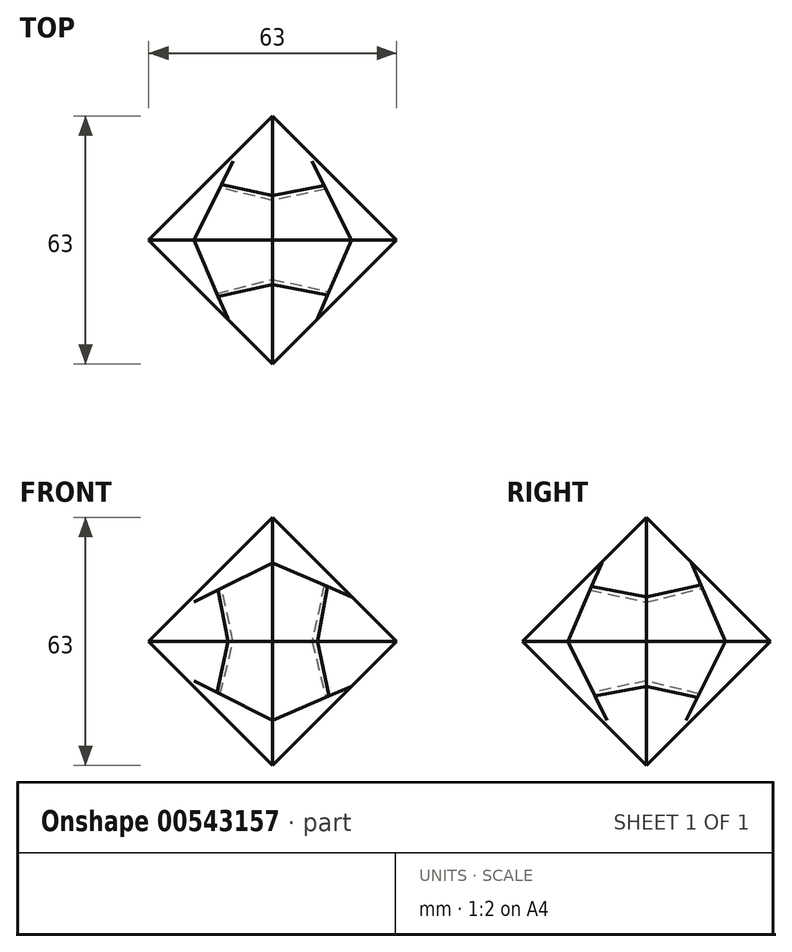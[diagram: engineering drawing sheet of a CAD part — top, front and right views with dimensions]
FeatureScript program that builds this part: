
annotation { "Feature Type Name" : "Feature", "Feature Type Description" : "" }
export const myFeature = defineFeature(function(context is Context, id is Id, definition is map)
    precondition{}
    {
        {
            var Q0;
            Q0=qCreatedBy(makeId("Front.planeOp"),FACE);
            var sketch = newSketch(context, id + "F0", { "sketchPlane" : qUnion([Q0])});
            skLineSegment(sketch, "E0", {"start": v(46.28, 0) * mm, "end": v(0, 20) * mm});
            skLineSegment(sketch, "E1", {"start": v(0, 20) * mm, "end": v(-40, 0) * mm});
            skLineSegment(sketch, "E2", {"start": v(-40, 0) * mm, "end": v(0, -20) * mm});
            skLineSegment(sketch, "E3", {"start": v(0, -20) * mm, "end": v(46.28, 0) * mm});
            skSolve(sketch);
        }
        {
            var Q0;
            Q0=makeQuery(id+"F0.imprint","IMPRINT",FACE,{"disambiguationData":[TD([[makeQuery(id+"F0.imprint","IMPRINT",EDGE,{"derivedFrom":sQuery(id+"F0.wireOp",EDGE,"E0")}),1.0]])]});
            extrude(context, id + "F1", {"entities" : qUnion([Q0]), "depth" : 25 * mm, "offsetDistance" : 25 * mm, "hasSecondDirection" : true, "secondDirectionOppositeDirection" : true, "secondDirectionDepth" : 25 * mm});
        }
        {
            var Q0;
            Q0=qCreatedBy(makeId("Front.planeOp"),FACE);
            var sketch = newSketch(context, id + "F2", { "sketchPlane" : qUnion([Q0])});
            skLineSegment(sketch, "E4", {"start": v(0, 49.78) * mm, "end": v(0, 0) * mm});
            skSolve(sketch);
        }
        {
            var Q0;
            Q0=qCreatedBy(makeId("Front.planeOp"),FACE);
            var sketch = newSketch(context, id + "F3", { "sketchPlane" : qUnion([Q0])});
            skLineSegment(sketch, "E5", {"start": v(60.84, 0) * mm, "end": v(0, 0) * mm});
            skSolve(sketch);
        }
        {
            var Q0;
            Q0=qCreatedBy(makeId("Right.planeOp"),FACE);
            var sketch = newSketch(context, id + "F4", { "sketchPlane" : qUnion([Q0])});
            skLineSegment(sketch, "E6", {"start": v(48.72, 0) * mm, "end": v(-1.84, 0) * mm});
            skSolve(sketch);
        }
        {
            var Q0;
            Q0=makeQuery(id+"F1.opExtrude","SWEPT_BODY",BODY,{"disambiguationData":[OSD([sQuery(id+"F0.wireOp",EDGE,"E0"),sQuery(id+"F0.wireOp",EDGE,"E1"),sQuery(id+"F0.wireOp",EDGE,"E2"),sQuery(id+"F0.wireOp",EDGE,"E3")])]});
            var Q1;
            Q1=sQuery(id+"F2.wireOp",EDGE,"E4");
            transform(context, id + "F5", {"entities" : qUnion([Q0]), "transformType" : TransformType.ROTATION, "transformAxis" : qUnion([Q1]), "angle" : 90 * degree, "makeCopy" : true});
        }
        {
            var Q0;
            Q0=makeQuery(id+"F5.opPattern","COPY",BODY,{"derivedFrom":makeQuery(id+"F1.opExtrude","SWEPT_BODY",BODY,{"disambiguationData":[OSD([sQuery(id+"F0.wireOp",EDGE,"E0"),sQuery(id+"F0.wireOp",EDGE,"E1"),sQuery(id+"F0.wireOp",EDGE,"E2"),sQuery(id+"F0.wireOp",EDGE,"E3")])]}),"instanceName":"1"});
            var Q1;
            Q1=sQuery(id+"F4.wireOp",EDGE,"E6");
            transform(context, id + "F6", {"entities" : qUnion([Q0]), "transformType" : TransformType.ROTATION, "transformAxis" : qUnion([Q1]), "angle" : 90 * degree, "makeCopy" : true});
        }
        {
            var Q0;
            Q0=makeQuery(id+"F5.opPattern","COPY",BODY,{"derivedFrom":makeQuery(id+"F1.opExtrude","SWEPT_BODY",BODY,{"disambiguationData":[OSD([sQuery(id+"F0.wireOp",EDGE,"E0"),sQuery(id+"F0.wireOp",EDGE,"E1"),sQuery(id+"F0.wireOp",EDGE,"E2"),sQuery(id+"F0.wireOp",EDGE,"E3")])]}),"instanceName":"1"});
            var Q1;
            Q1=sQuery(id+"F3.wireOp",EDGE,"E5");
            transform(context, id + "F7", {"entities" : qUnion([Q0]), "transformType" : TransformType.ROTATION, "transformAxis" : qUnion([Q1]), "angle" : 90 * degree, "makeCopy" : false});
        }
        {
            var Q0;
            Q0=makeQuery(id+"F5.opPattern","COPY",BODY,{"derivedFrom":makeQuery(id+"F1.opExtrude","SWEPT_BODY",BODY,{"disambiguationData":[OSD([sQuery(id+"F0.wireOp",EDGE,"E0"),sQuery(id+"F0.wireOp",EDGE,"E1"),sQuery(id+"F0.wireOp",EDGE,"E2"),sQuery(id+"F0.wireOp",EDGE,"E3")])]}),"instanceName":"1"});
            var Q1;
            Q1=makeQuery(id+"F6.opPattern","COPY",BODY,{"derivedFrom":makeQuery(id+"F5.opPattern","COPY",BODY,{"derivedFrom":makeQuery(id+"F1.opExtrude","SWEPT_BODY",BODY,{"disambiguationData":[OSD([sQuery(id+"F0.wireOp",EDGE,"E0"),sQuery(id+"F0.wireOp",EDGE,"E1"),sQuery(id+"F0.wireOp",EDGE,"E2"),sQuery(id+"F0.wireOp",EDGE,"E3")])]}),"instanceName":"1"}),"instanceName":"1"});
            booleanBodies(context, id + "F8", {"operationType" : BooleanOperationType.INTERSECTION, "tools" : qUnion([Q0, Q1])});
        }
        {
            var Q0;
            {var subQ0=makeQuery(id+"F5.opPattern","COPY",BODY,{"derivedFrom":makeQuery(id+"F1.opExtrude","SWEPT_BODY",BODY,{"disambiguationData":[OSD([sQuery(id+"F0.wireOp",EDGE,"E0"),sQuery(id+"F0.wireOp",EDGE,"E1"),sQuery(id+"F0.wireOp",EDGE,"E2"),sQuery(id+"F0.wireOp",EDGE,"E3")])]}),"instanceName":"1"});Q0=makeQuery(id+"F8.opBoolean","INTERSECT",BODY,{"derivedFrom":[subQ0,makeQuery(id+"F6.opPattern","COPY",BODY,{"derivedFrom":subQ0,"instanceName":"1"})]});}
            var Q1;
            Q1=makeQuery(id+"F1.opExtrude","SWEPT_BODY",BODY,{"disambiguationData":[OSD([sQuery(id+"F0.wireOp",EDGE,"E0"),sQuery(id+"F0.wireOp",EDGE,"E1"),sQuery(id+"F0.wireOp",EDGE,"E2"),sQuery(id+"F0.wireOp",EDGE,"E3")])]});
            booleanBodies(context, id + "F9", {"operationType" : BooleanOperationType.INTERSECTION, "tools" : qUnion([Q0, Q1])});
        }
        {
            var Q0;
            Q0=qCreatedBy(makeId("Top.planeOp"),FACE);
            var sketch = newSketch(context, id + "F10", { "sketchPlane" : qUnion([Q0])});
            skLineSegment(sketch, "E7", {"start": v(20, 0) * mm, "end": v(0, 20) * mm});
            skLineSegment(sketch, "E8", {"start": v(0, 20) * mm, "end": v(-20, 0) * mm});
            skLineSegment(sketch, "E9", {"start": v(-20, 0) * mm, "end": v(0, -20) * mm});
            skLineSegment(sketch, "E10", {"start": v(0, -20) * mm, "end": v(20, 0) * mm});
            skSolve(sketch);
        }
        {
            var Q0;
            Q0 = qSketchRegion(id + "F10", true);
            extrude(context, id + "F11", {"entities" : qUnion([Q0]), "depth" : 20 * mm, "offsetDistance" : 25 * mm, "hasDraft" : true, "draftAngle" : atan(1 / sqrt(2)), "draftPullDirection" : true, "hasSecondDirection" : true, "secondDirectionOppositeDirection" : true, "secondDirectionDepth" : 20 * mm, "hasSecondDirectionDraft" : true, "secondDirectionDraftAngle" : atan(1 / sqrt(2)), "secondDirectionDraftPullDirection" : true});
        }
        {
            var Q0;
            {var subQ0=makeQuery(id+"F1.opExtrude","SWEPT_BODY",BODY,{"disambiguationData":[OSD([sQuery(id+"F0.wireOp",EDGE,"E0"),sQuery(id+"F0.wireOp",EDGE,"E1"),sQuery(id+"F0.wireOp",EDGE,"E2"),sQuery(id+"F0.wireOp",EDGE,"E3")])]});var subQ1=makeQuery(id+"F5.opPattern","COPY",BODY,{"derivedFrom":subQ0,"instanceName":"1"});Q0=makeQuery(id+"F9.opBoolean","INTERSECT",BODY,{"derivedFrom":[subQ0,makeQuery(id+"F8.opBoolean","INTERSECT",BODY,{"derivedFrom":[subQ1,makeQuery(id+"F6.opPattern","COPY",BODY,{"derivedFrom":subQ1,"instanceName":"1"})]})]});}
            transform(context, id + "F12", {"entities" : qUnion([Q0]), "transformType" : TransformType.TRANSLATION_3D, "dx" : 50 * mm, "dy" : 0 * mm, "dz" : 0 * mm, "makeCopy" : false});
        }
        {
            var Q0;
            Q0=makeQuery(id+"F11.*.split.splitOp","SPLIT",BODY,{"derivedFrom":makeQuery(id+"F11.opExtrude","SWEPT_BODY",BODY,{"disambiguationData":[OSD([sQuery(id+"F10.wireOp",EDGE,"E7"),sQuery(id+"F10.wireOp",EDGE,"E8"),sQuery(id+"F10.wireOp",EDGE,"E9"),sQuery(id+"F10.wireOp",EDGE,"E10")])]})});
            var Q1;
            Q1=qCreatedBy(makeId("Origin.pointOp"),VERTEX);
            transform(context, id + "F13", {"entities" : qUnion([Q0]), "transformType" : TransformType.SCALE_UNIFORMLY, "scale" : 1.5, "scalePoint" : qUnion([Q1]), "makeCopy" : false});
        }
        {
            var Q0;
            {var subQ0=makeQuery(id+"F1.opExtrude","SWEPT_BODY",BODY,{"disambiguationData":[OSD([sQuery(id+"F0.wireOp",EDGE,"E0"),sQuery(id+"F0.wireOp",EDGE,"E1"),sQuery(id+"F0.wireOp",EDGE,"E2"),sQuery(id+"F0.wireOp",EDGE,"E3")])]});var subQ1=makeQuery(id+"F5.opPattern","COPY",BODY,{"derivedFrom":subQ0,"instanceName":"1"});Q0=makeQuery(id+"F9.opBoolean","INTERSECT",BODY,{"derivedFrom":[subQ0,makeQuery(id+"F8.opBoolean","INTERSECT",BODY,{"derivedFrom":[subQ1,makeQuery(id+"F6.opPattern","COPY",BODY,{"derivedFrom":subQ1,"instanceName":"1"})]})]});}
            transform(context, id + "F14", {"entities" : qUnion([Q0]), "transformType" : TransformType.TRANSLATION_3D, "dx" : -50 * mm, "dy" : 0 * mm, "dz" : 0 * mm, "makeCopy" : false});
        }
        {
            var Q0;
            Q0=makeQuery(id+"F11.*.split.splitOp","SPLIT",BODY,{"derivedFrom":makeQuery(id+"F11.opExtrude","SWEPT_BODY",BODY,{"disambiguationData":[OSD([sQuery(id+"F10.wireOp",EDGE,"E7"),sQuery(id+"F10.wireOp",EDGE,"E8"),sQuery(id+"F10.wireOp",EDGE,"E9"),sQuery(id+"F10.wireOp",EDGE,"E10")])]})});
            var Q1;
            Q1=qCreatedBy(makeId("Origin.pointOp"),VERTEX);
            transform(context, id + "F15", {"entities" : qUnion([Q0]), "transformType" : TransformType.SCALE_UNIFORMLY, "scale" : 1.05, "scalePoint" : qUnion([Q1]), "makeCopy" : false});
        }
    });
